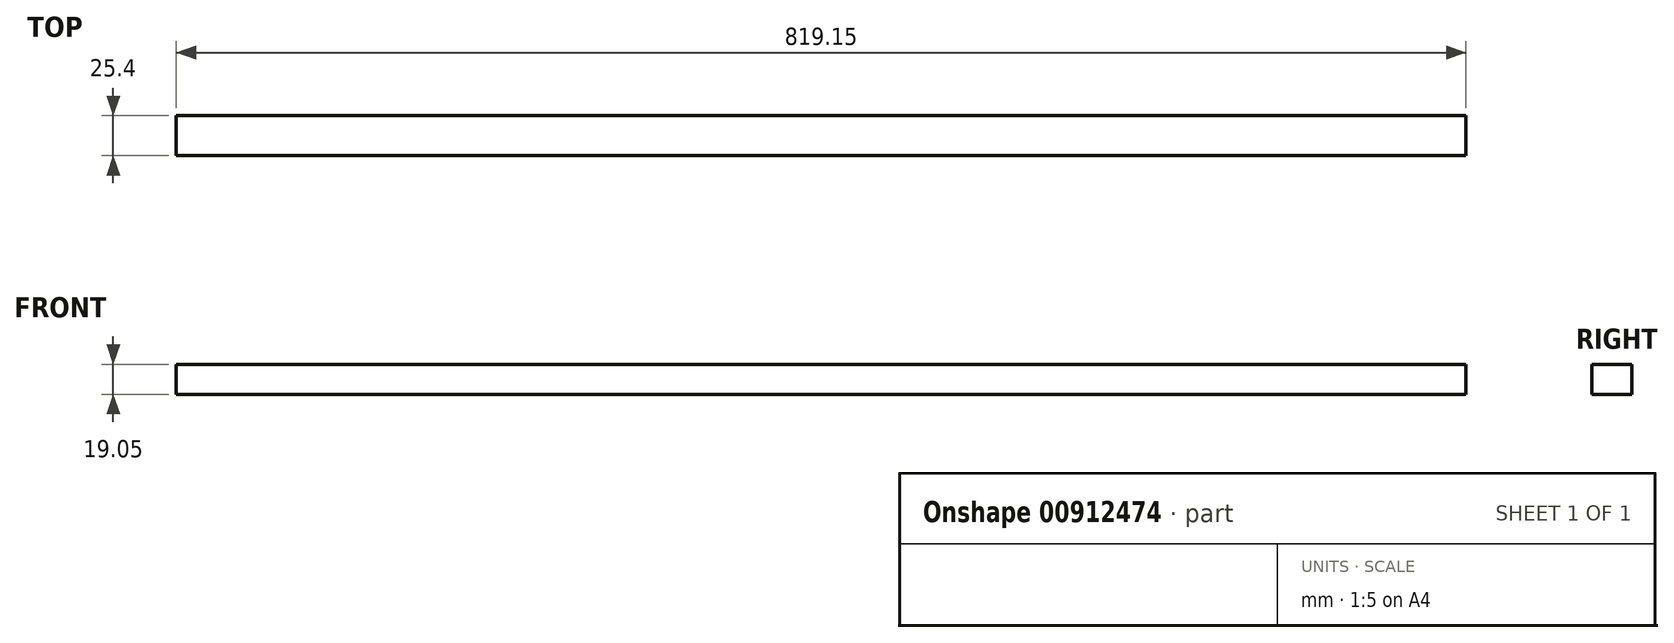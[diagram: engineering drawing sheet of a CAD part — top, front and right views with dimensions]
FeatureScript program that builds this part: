
annotation { "Feature Type Name" : "Feature", "Feature Type Description" : "" }
export const myFeature = defineFeature(function(context is Context, id is Id, definition is map)
    precondition{}
    {
        {
            var Q0;
            Q0=qCreatedBy(makeId("Front.planeOp"),FACE);
            var sketch = newSketch(context, id + "F0", { "sketchPlane" : qUnion([Q0])});
            skLineSegment(sketch, "E0.bottom", {"start": v(0, 0) * mm, "end": v(819.15, 0) * mm});
            skLineSegment(sketch, "E0.top", {"start": v(0, 19.05) * mm, "end": v(819.15, 19.05) * mm});
            skLineSegment(sketch, "E0.left", {"start": v(0, 0) * mm, "end": v(0, 19.05) * mm});
            skLineSegment(sketch, "E0.right", {"start": v(819.15, 0) * mm, "end": v(819.15, 19.05) * mm});
            skSolve(sketch);
        }
        {
            var Q0;
            Q0 = qSketchRegion(id + "F0", true);
            extrude(context, id + "F1", {"entities" : qUnion([Q0]), "depth" : 25.4 * mm, "offsetDistance" : 25.4 * mm});
        }
    });
